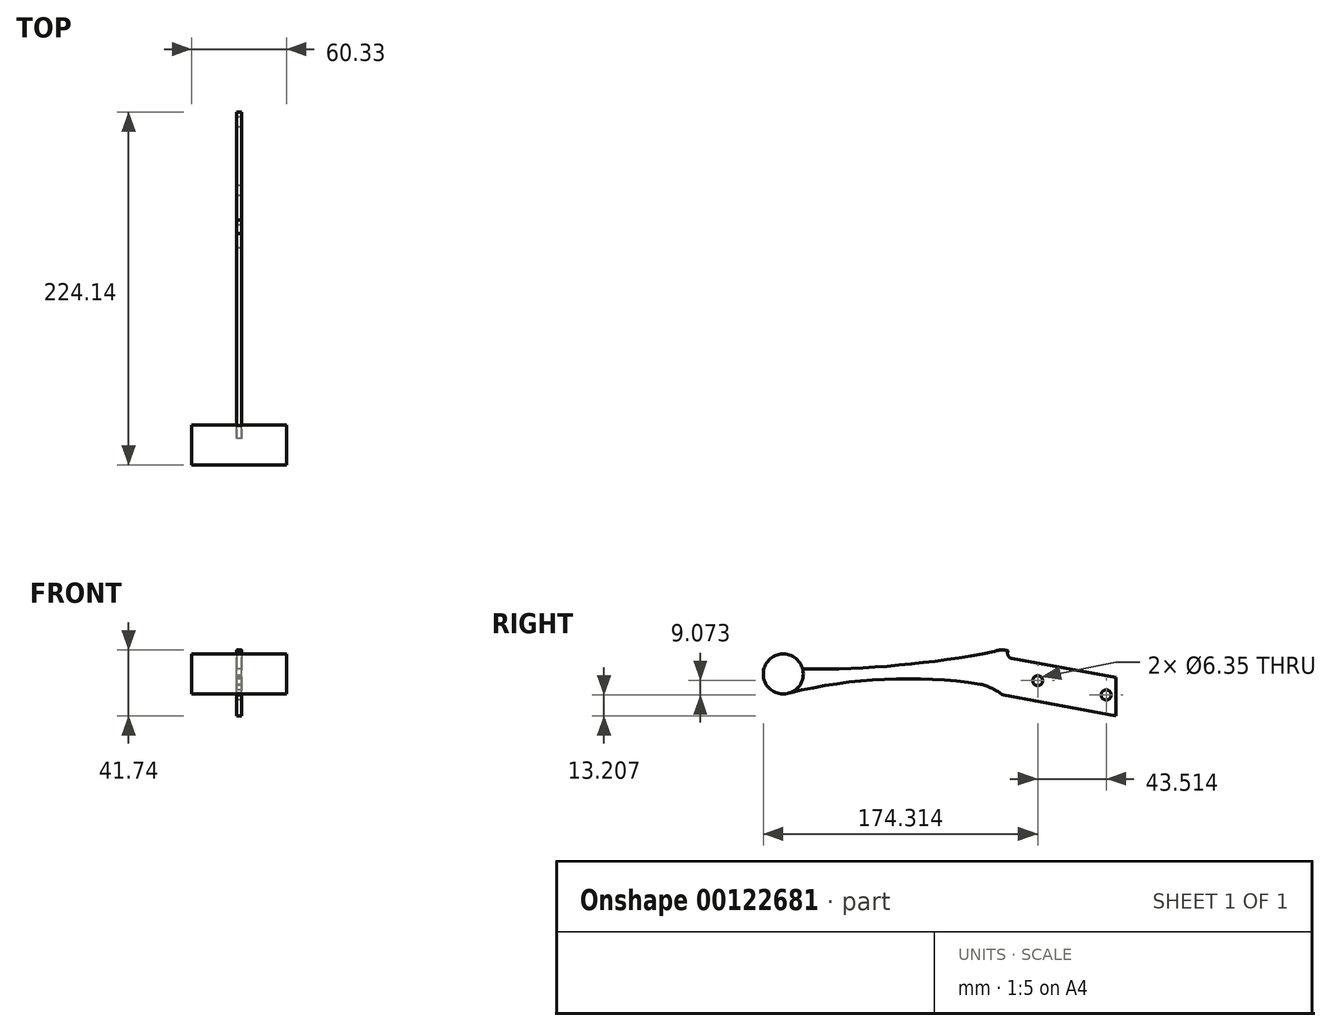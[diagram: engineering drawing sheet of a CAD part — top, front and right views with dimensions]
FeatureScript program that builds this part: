
annotation { "Feature Type Name" : "Feature", "Feature Type Description" : "" }
export const myFeature = defineFeature(function(context is Context, id is Id, definition is map)
    precondition{}
    {
        {
            var Q0;
            Q0=qCreatedBy(makeId("Right.planeOp"),FACE);
            var sketch = newSketch(context, id + "F0", { "sketchPlane" : qUnion([Q0])});
            skLineSegment(sketch, "E0", {"start": v(199.84, -52.71) * mm, "end": v(265.88, -64.76) * mm});
            skLineSegment(sketch, "E1", {"start": v(265.88, -64.76) * mm, "end": v(265.88, -88.97) * mm});
            skLineSegment(sketch, "E2", {"start": v(265.88, -88.97) * mm, "end": v(194.22, -75.9) * mm});
            skCircle(sketch, "E3", {"center": v(54.44, -62.49) * mm, "radius": 4.76 * mm});
            skCircle(sketch, "E4", {"center": v(216.05, -66.69) * mm, "radius": 3.18 * mm});
            skCircle(sketch, "E5", {"center": v(259.57, -75.76) * mm, "radius": 3.18 * mm});
            skArc(sketch, "E6", {"start": v(66.74, -59.33) * mm, "mid": v(43.23, -56.52) * mm, "end": v(58.69, -74.45) * mm});
            skArc(sketch, "E7", {"start": v(179.54, -68.93) * mm, "mid": v(118.84, -65.77) * mm, "end": v(58.69, -74.45) * mm});
            skArc(sketch, "E8", {"start": v(197.27, -47.77) * mm, "mid": v(192.9, -47.24) * mm, "end": v(188.61, -48.2) * mm});
            skArc(sketch, "E9", {"start": v(197.27, -47.77) * mm, "mid": v(197.34, -50.87) * mm, "end": v(199.84, -52.71) * mm});
            skArc(sketch, "E10", {"start": v(194.22, -75.9) * mm, "mid": v(187.2, -71.73) * mm, "end": v(179.54, -68.93) * mm});
            skArc(sketch, "E11", {"start": v(66.74, -59.33) * mm, "mid": v(127.96, -56.86) * mm, "end": v(188.61, -48.2) * mm});
            skLineSegment(sketch, "E12", {"start": v(199.84, -52.71) * mm, "end": v(194.22, -75.9) * mm});
            skSolve(sketch);
        }
        {
            var Q0;
            Q0=makeQuery(id+"F0.imprint","IMPRINT",FACE,{"disambiguationData":[TD([[makeQuery(id+"F0.imprint","IMPRINT",EDGE,{"derivedFrom":sQuery(id+"F0.wireOp",EDGE,"E3")}),-1.0]])]});
            var Q1;
            Q1=makeQuery(id+"F0.imprint","IMPRINT",FACE,{"disambiguationData":[TD([[makeQuery(id+"F0.imprint","IMPRINT",EDGE,{"derivedFrom":sQuery(id+"F0.wireOp",EDGE,"E0")}),-1.0]])]});
            extrude(context, id + "F1", {"entities" : qUnion([Q0, Q1]), "depth" : 3.17 * mm});
        }
        {
            var Q0;
            Q0=qCreatedBy(makeId("Right.planeOp"),FACE);
            var sketch = newSketch(context, id + "F2", { "sketchPlane" : qUnion([Q0])});
            skCircle(sketch, "E13", {"center": v(54.44, -62.49) * mm, "radius": 12.7 * mm});
            skSolve(sketch);
        }
        {
            var Q0;
            Q0 = qSketchRegion(id + "F2", true);
            extrude(context, id + "F3", {"entities" : qUnion([Q0]), "operationType" : NewBodyOperationType.ADD, "depth" : 31.75 * mm, "hasSecondDirection" : true, "secondDirectionOppositeDirection" : true, "secondDirectionDepth" : 28.57 * mm});
        }
    });
